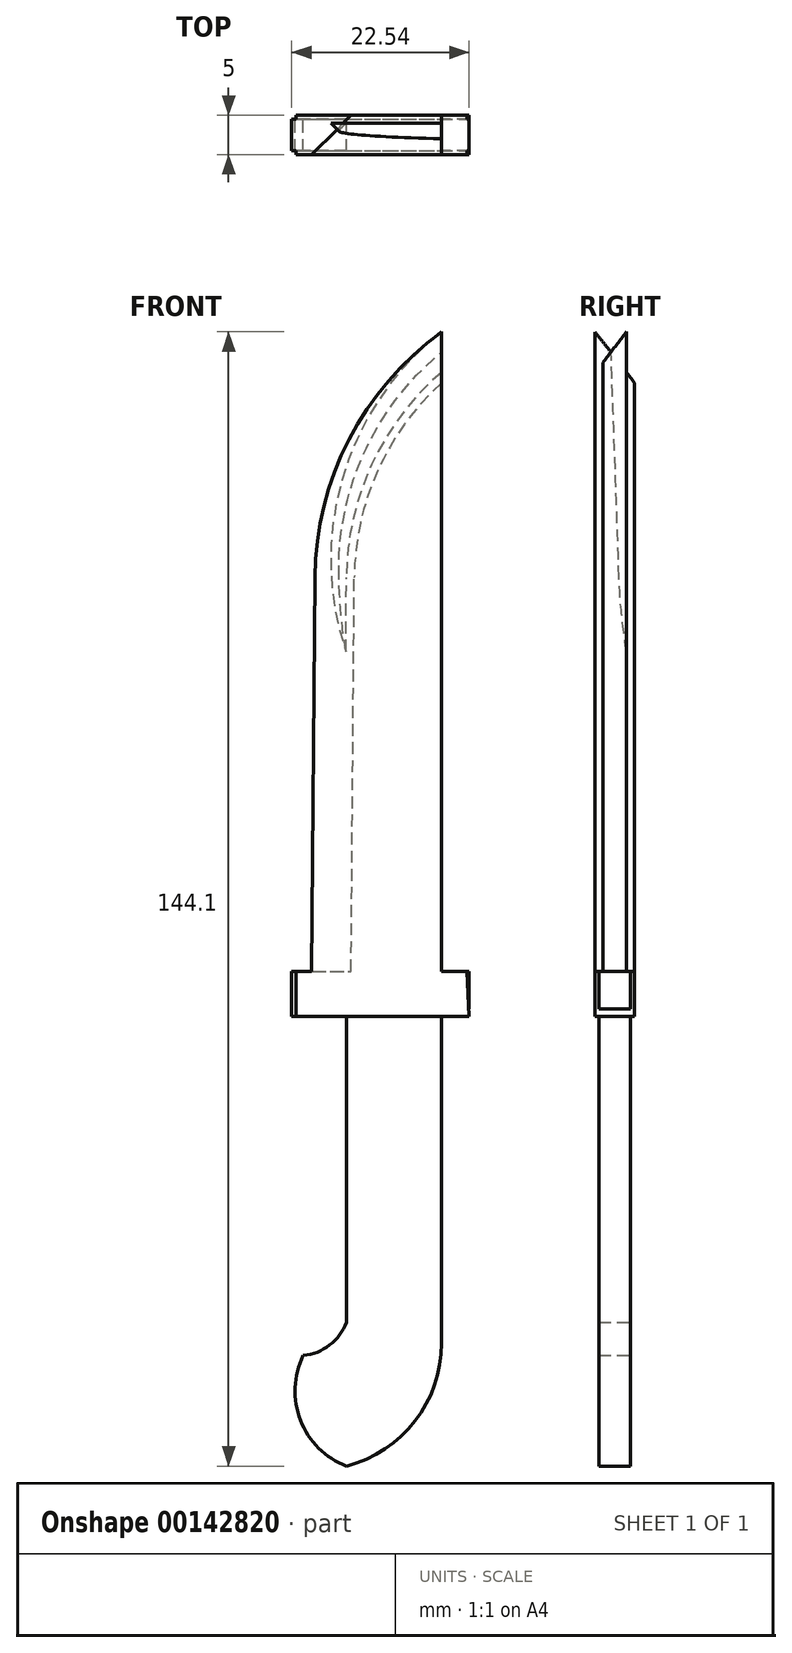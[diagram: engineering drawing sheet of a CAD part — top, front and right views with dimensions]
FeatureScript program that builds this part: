
annotation { "Feature Type Name" : "Feature", "Feature Type Description" : "" }
export const myFeature = defineFeature(function(context is Context, id is Id, definition is map)
    precondition{}
    {
        {
            var Q0;
            Q0=qCreatedBy(makeId("Front.planeOp"),FACE);
            var sketch = newSketch(context, id + "F0", { "sketchPlane" : qUnion([Q0])});
            skLineSegment(sketch, "E0", {"start": v(0, 55) * mm, "end": v(0, 0) * mm});
            skLineSegment(sketch, "E1", {"start": v(0, 0) * mm, "end": v(-16.49, 0) * mm});
            skLineSegment(sketch, "E2", {"start": v(-16.49, 0) * mm, "end": v(-16.07, 52.61) * mm});
            skArc(sketch, "E3", {"start": v(0, 83.74) * mm, "mid": v(-11.75, 70.09) * mm, "end": v(-16.07, 52.61) * mm});
            skLineSegment(sketch, "E4", {"start": v(0, 83.74) * mm, "end": v(0, 55) * mm});
            skSolve(sketch);
        }
        {
            var Q0;
            Q0=makeQuery(id+"F0.imprint","IMPRINT",FACE,{"disambiguationData":[TD([[makeQuery(id+"F0.imprint","IMPRINT",EDGE,{"derivedFrom":sQuery(id+"F0.wireOp",EDGE,"E0")}),-1.0]])]});
            extrude(context, id + "F1", {"entities" : qUnion([Q0]), "endBound" : BoundingType.SYMMETRIC, "depth" : 3 * mm});
        }
        {
            var Q0;
            Q0=makeQuery(id+"F1.opExtrude","CAP_EDGE",EDGE,{"disambiguationData":[OSD([sQuery(id+"F0.wireOp",EDGE,"E3")])],"isStart":false});
            chamfer(context, id + "F2", {"entities" : qUnion([Q0]), "width" : 5 * mm, "tangentPropagation" : true});
        }
        {
            var Q0;
            Q0=qCreatedBy(makeId("Front.planeOp"),FACE);
            var sketch = newSketch(context, id + "F3", { "sketchPlane" : qUnion([Q0])});
            skLineSegment(sketch, "E5", {"start": v(0, 0) * mm, "end": v(3.46, 0) * mm});
            skLineSegment(sketch, "E6", {"start": v(3.46, 0) * mm, "end": v(3.46, -5.77) * mm});
            skLineSegment(sketch, "E7", {"start": v(3.46, -5.77) * mm, "end": v(-19.03, -5.77) * mm});
            skLineSegment(sketch, "E8", {"start": v(-19.03, -5.77) * mm, "end": v(-19.03, 0) * mm});
            skLineSegment(sketch, "E9", {"start": v(-19.03, 0) * mm, "end": v(3.46, 0) * mm});
            skLineSegment(sketch, "E10", {"start": v(0, -5.77) * mm, "end": v(0, -47.29) * mm});
            skLineSegment(sketch, "E11", {"start": v(-12.07, -5.77) * mm, "end": v(-12.07, -47.29) * mm});
            skArc(sketch, "E12", {"start": v(-17.57, -48.82) * mm, "mid": v(-12.63, -45.74) * mm, "end": v(-12.07, -39.96) * mm});
            skArc(sketch, "E13", {"start": v(-12.07, -62.87) * mm, "mid": v(-3.37, -57.14) * mm, "end": v(0, -47.29) * mm});
            skArc(sketch, "E14", {"start": v(-17.57, -48.82) * mm, "mid": v(-17.92, -57.05) * mm, "end": v(-12.07, -62.87) * mm});
            skSolve(sketch);
        }
        {
            var Q0;
            Q0 = qSketchRegion(id + "F3", true);
            extrude(context, id + "F4", {"entities" : qUnion([Q0]), "operationType" : NewBodyOperationType.ADD, "endBound" : BoundingType.SYMMETRIC, "depth" : 4 * mm});
        }
        {
            var Q0;
            Q0=qCreatedBy(makeId("Front.planeOp"),FACE);
            var sketch = newSketch(context, id + "F5", { "sketchPlane" : qUnion([Q0])});
            skLineSegment(sketch, "E15", {"start": v(0, 0) * mm, "end": v(3.2, 0) * mm});
            skLineSegment(sketch, "E16", {"start": v(3.2, 0) * mm, "end": v(3.51, -5.74) * mm});
            skLineSegment(sketch, "E17", {"start": v(3.51, -5.74) * mm, "end": v(-18.48, -5.74) * mm});
            skLineSegment(sketch, "E18", {"start": v(-18.48, -5.74) * mm, "end": v(-18.48, 0) * mm});
            skLineSegment(sketch, "E19", {"start": v(-18.48, 0) * mm, "end": v(3.2, 0) * mm});
            skSolve(sketch);
        }
        {
            var Q0;
            Q0 = qSketchRegion(id + "F5", true);
            extrude(context, id + "F6", {"entities" : qUnion([Q0]), "operationType" : NewBodyOperationType.ADD, "endBound" : BoundingType.SYMMETRIC, "depth" : 5 * mm});
        }
        {
            var Q0;
            Q0=qCreatedBy(makeId("Front.planeOp"),FACE);
            var sketch = newSketch(context, id + "F7", { "sketchPlane" : qUnion([Q0])});
            skLineSegment(sketch, "E20", {"start": v(-0.02, 68.92) * mm, "end": v(-0.02, -2.57) * mm});
            skLineSegment(sketch, "E21", {"start": v(-0.02, -2.57) * mm, "end": v(-16.5, -2.57) * mm});
            skLineSegment(sketch, "E22", {"start": v(-16.5, -2.57) * mm, "end": v(-16.09, 50.04) * mm});
            skArc(sketch, "E23", {"start": v(-0.02, 81.17) * mm, "mid": v(-11.77, 67.52) * mm, "end": v(-16.09, 50.04) * mm});
            skLineSegment(sketch, "E24", {"start": v(-0.02, 81.17) * mm, "end": v(-0.02, 68.92) * mm});
            skSolve(sketch);
        }
        {
            var Q0;
            Q0 = qSketchRegion(id + "F7", true);
            extrude(context, id + "F8", {"entities" : qUnion([Q0]), "operationType" : NewBodyOperationType.ADD, "endBound" : BoundingType.SYMMETRIC, "depth" : 5 * mm});
        }
        {
            var Q0;
            Q0=makeQuery(id+"F8.opExtrude","CAP_EDGE",EDGE,{"disambiguationData":[OSD([sQuery(id+"F7.wireOp",EDGE,"E22")])],"isStart":true});
            chamfer(context, id + "F9", {"entities" : qUnion([Q0]), "width" : 5 * mm, "tangentPropagation" : true});
        }
    });
